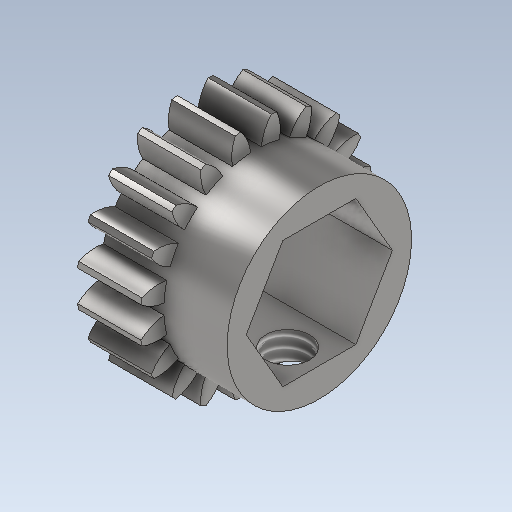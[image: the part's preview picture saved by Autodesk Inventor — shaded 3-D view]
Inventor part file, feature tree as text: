
AUTODESK INVENTOR PART (.ipt)
format: ipt  version: 2023 (Build 270158000, 158)  size: 347,136 bytes
history: native  units: in
note: dims shown in document units (in); Inventor stores cm internally (conversion verified against a paired STEP export)
features: other x3, sketch x2
ambient origin geometry x8: Origin, YZ Plane, XZ Plane, XY Plane, X Axis, Y Axis, Z Axis, Center Point
bodies: Solid1 (feature_tree)
feature tree (5):
  other  "CH-1-01-20T_Idler.ipt"
  other  "Solid1::CH-1-01-20T_Idler.ipt"
  other  "TaggingFeature1"
  sketch  "Sketch3"  dims[d0=0.3937in]
  sketch  "Sketch4"
